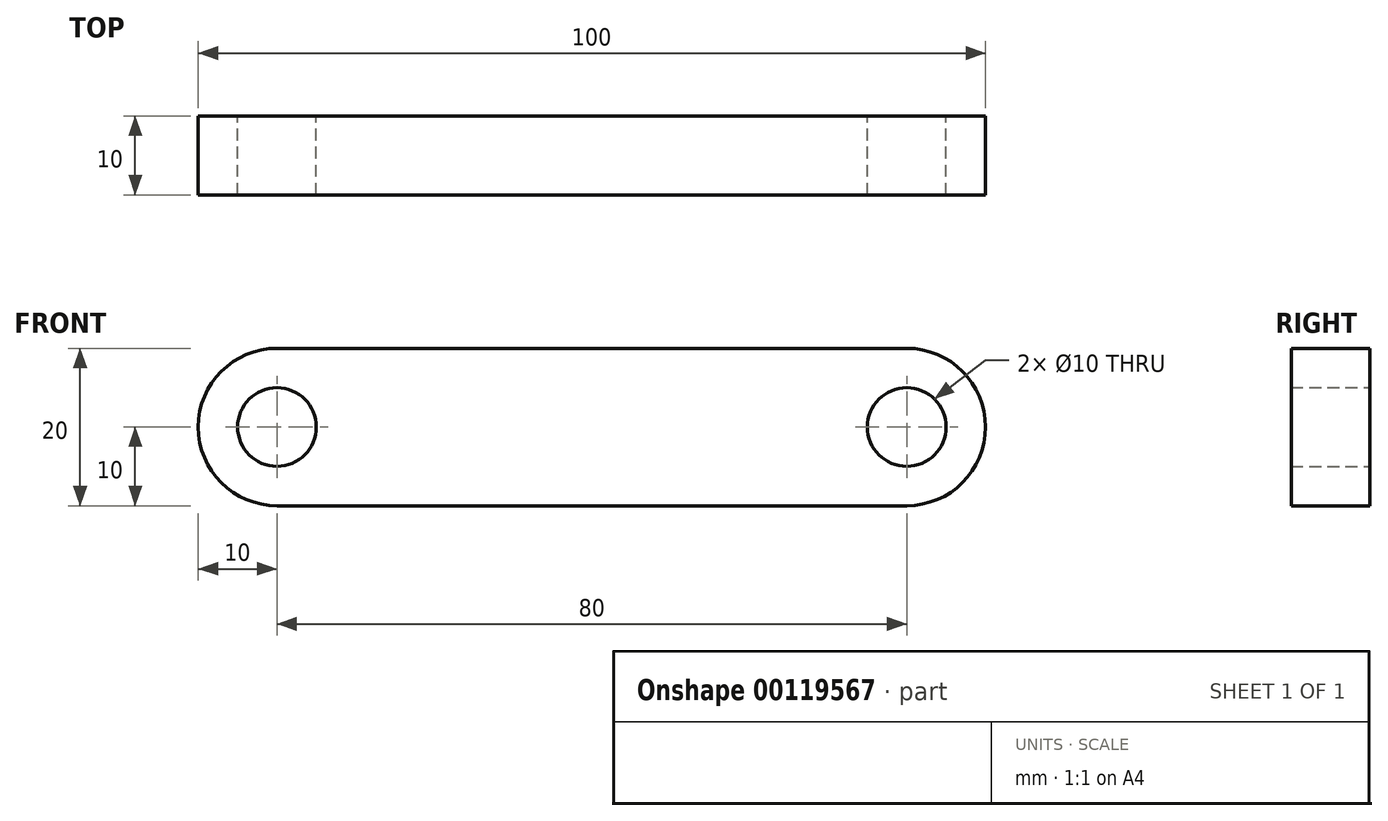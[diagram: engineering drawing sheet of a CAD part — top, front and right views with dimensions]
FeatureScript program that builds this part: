
annotation { "Feature Type Name" : "Feature", "Feature Type Description" : "" }
export const myFeature = defineFeature(function(context is Context, id is Id, definition is map)
    precondition{}
    {
        {
            var Q0;
            Q0=qCreatedBy(makeId("Front.planeOp"),FACE);
            var sketch = newSketch(context, id + "F0", { "sketchPlane" : qUnion([Q0])});
            skLineSegment(sketch, "E0", {"start": v(0, 0) * mm, "end": v(80, 0) * mm});
            skArc(sketch, "E1", {"start": v(80, 0) * mm, "mid": v(90, -10) * mm, "end": v(80, -20) * mm});
            skLineSegment(sketch, "E2", {"start": v(80, -20) * mm, "end": v(0, -20) * mm});
            skArc(sketch, "E3", {"start": v(0, -20) * mm, "mid": v(-10, -10) * mm, "end": v(0, 0) * mm});
            skCircle(sketch, "E4", {"center": v(0, -10) * mm, "radius": 5 * mm});
            skCircle(sketch, "E5", {"center": v(80, -10) * mm, "radius": 5 * mm});
            skSolve(sketch);
        }
        {
            var Q0;
            Q0 = qSketchRegion(id + "F0", true);
            extrude(context, id + "F1", {"entities" : qUnion([Q0]), "depth" : 10 * mm});
        }
    });
